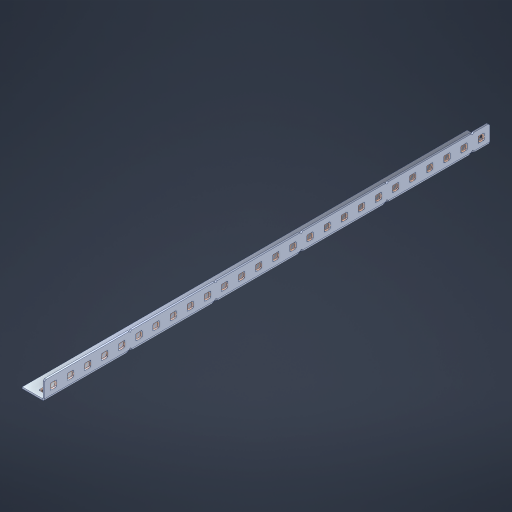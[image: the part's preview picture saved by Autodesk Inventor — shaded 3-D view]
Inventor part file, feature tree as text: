
AUTODESK INVENTOR PART (.ipt)
format: ipt  version: 2023 (Build 270158000, 158)  size: 876,544 bytes
history: native  units: in
note: dims shown in document units (in); Inventor stores cm internally (conversion verified against a paired STEP export)
features: other x57, extrude x51, sheet_metal_op x10, sketch x8, mirror x1, pattern_linear x1, chamfer x1
ambient origin geometry x8: Origin, YZ Plane, XZ Plane, XY Plane, X Axis, Y Axis, Z Axis, Center Point
bodies: Solid1 (feature_tree), Body (feature_tree)
feature tree (129):
  other  "Flange Pattern Plane"
  sheet_metal_op  "Flange Pattern"
  sheet_metal_op  "Body Pattern"
  other  "Arc Length"
  mirror  "Notch Mirror"
  pattern_linear  "Notch Pattern"  Spacing1=0.1875in  [1 undecoded]
  chamfer  "End Chamfer"
  extrude  "Half Cut"  Depth=0.0469in
  sketch  "Sketch1"  dims[d0=2.5in]
  other  "Plate1"
  sketch  "Sketch2"  dims[d1=13.0in]
  other  "Plate2"
  sheet_metal_op  "Bend1"
  sheet_metal_op  "Corner1"
  sketch  "Sketch3"  dims[d2=0.0469in]
  other  "Flange Pattern Sketch"
  sketch  "Sketch7"  dims[d3=0.0469in]
  other  "Srf1"
  other  "Srf2"
  sketch  "Sketch8"  dims[d4=0.0234in]
  sketch  "Sketch9"  dims[d5=0.0938in]
  other  "Srf91"
  sheet_metal_op  "Body Pattern Sketch"
  other  "Srf92"
  sketch  "Sketch13"  dims[d6=0.0469in]
  sketch  "Sketch14"  dims[d7=0.5in d8=90.0deg d9=0.0312in d10=0.1875in d11=0.0469in d12=0.0469in d16=0.182in d17=0.02in d18=0.0469in d19=0.0in d20=0.25in d21=0.25in d46=0.172in d47=1.0in d48=0.0in d49=0.182in d50=0.02in d51=0.25in d52=0.25in d53=0.0469in d54=0.0in d55=0.172in d56=1.0in d57=0.0in d60=10.2362in d62=0.5in d63=0.3937in d65=0.5in d85=0.1227in d86=0.1659in d88=0.04in d89=0.0469in d90=0.0in d91=0.04in d92=0.0491in d95=2.5in d96=0.04in d97=0.25in d98=45.0deg d101=0.0in d102=2.497in d131=0.5in d132=10.2362in d134=0.5in d139=0.5in]
  other  "Srf856"
  other  "Srf1310"
  other  "Srf1311"
  other  "Srf1312"
  other  "Srf1376"
  other  "Srf1377"
  other  "Srf1728"
  other  "Srf1755"
  other  "Srf1878"
  other  "Srf1879"
  other  "Srf1880"
  other  "Srf1881"
  other  "Srf1882"
  other  "Srf1883"
  other  "Srf1884"
  other  "Srf1885"
  other  "Srf1886"
  other  "Srf1887"
  other  "Srf1888"
  other  "Srf1889"
  other  "Srf1890"
  other  "Srf1891"
  other  "Srf1892"
  other  "Srf1893"
  other  "Srf1894"
  other  "Srf1895"
  other  "Srf1896"
  other  "Srf1897"
  other  "Srf1942"
  other  "Srf1943"
  other  "Srf1944"
  other  "Srf1945"
  other  "Srf1946"
  other  "Srf1947"
  other  "Srf1948"
  other  "Srf1949"
  other  "Srf1950"
  other  "Srf1951"
  other  "Srf1952"
  other  "Srf1953"
  other  "Srf1954"
  other  "Srf1955"
  other  "Srf1956"
  other  "Srf1957"
  other  "Srf1958"
  other  "Srf1959"
  other  "Srf1960"
  other  "Srf1961"
  sheet_metal_op  "Flange Stamp"
  sheet_metal_op  "Flange Circle"
  sheet_metal_op  "Body Stamp"
  sheet_metal_op  "Body Circle"
  sheet_metal_op  "Notch"
  extrude  "ExtrusionSrf2"  Depth=0.0469in
  extrude  "ExtrusionSrf92"  Depth=0.5in
  extrude  "ExtrusionSrf856"  Depth=0.02in
  extrude  "ExtrusionSrf1310"  Depth=0.0469in
  extrude  "ExtrusionSrf1311"  TaperAngle=0.0deg  [1 undecoded]
  extrude  "ExtrusionSrf1312"  Depth=0.5in
  extrude  "ExtrusionSrf1376"  Depth=0.5in
  extrude  "ExtrusionSrf1377"  Depth=0.5in
  extrude  "ExtrusionSrf1728"  Depth=0.5in TaperAngle=0.0deg
  extrude  "ExtrusionSrf1755"  Depth=0.5in
  extrude  "ExtrusionSrf1878"  Depth=0.02in
  extrude  "ExtrusionSrf1879"  Depth=0.5in
  extrude  "ExtrusionSrf1880"  Depth=0.5in
  extrude  "ExtrusionSrf1881"  Depth=0.0469in
  extrude  "ExtrusionSrf1882"  TaperAngle=0.0deg  [1 undecoded]
  extrude  "ExtrusionSrf1883"  Depth=0.5in
  extrude  "ExtrusionSrf1884"  Depth=0.5in TaperAngle=0.0deg
  extrude  "ExtrusionSrf1885"  Depth=0.5in
  extrude  "ExtrusionSrf1886"  Depth=0.5in
  extrude  "ExtrusionSrf1887"  Depth=0.5in
  extrude  "ExtrusionSrf1888"  Depth=0.5in
  extrude  "ExtrusionSrf1889"  Depth=0.5in
  extrude  "ExtrusionSrf1890"  Depth=0.0469in
  extrude  "ExtrusionSrf1891"  TaperAngle=0.0deg  [1 undecoded]
  extrude  "ExtrusionSrf1892"  Depth=0.5in
  extrude  "ExtrusionSrf1893"  Depth=0.5in
  extrude  "ExtrusionSrf1894"  Depth=0.5in
  extrude  "ExtrusionSrf1895"  Depth=0.5in TaperAngle=45.0deg
  extrude  "ExtrusionSrf1896"  TaperAngle=0.0deg  [1 undecoded]
  extrude  "ExtrusionSrf1897"  Depth=0.5in
  extrude  "ExtrusionSrf1942"  Depth=0.5in
  extrude  "ExtrusionSrf1943"  Depth=0.5in
  extrude  "ExtrusionSrf1944"  Depth=0.5in
  extrude  "ExtrusionSrf1945"  Depth=0.5in
  extrude  "ExtrusionSrf1946"  [1 undecoded]
  extrude  "ExtrusionSrf1947"  [1 undecoded]
  extrude  "ExtrusionSrf1948"  [1 undecoded]
  extrude  "ExtrusionSrf1949"  [1 undecoded]
  extrude  "ExtrusionSrf1950"  [1 undecoded]
  extrude  "ExtrusionSrf1951"  [1 undecoded]
  extrude  "ExtrusionSrf1952"  [1 undecoded]
  extrude  "ExtrusionSrf1953"  [1 undecoded]
  extrude  "ExtrusionSrf1954"  [1 undecoded]
  extrude  "ExtrusionSrf1955"  [1 undecoded]
  extrude  "ExtrusionSrf1956"  [1 undecoded]
  extrude  "ExtrusionSrf1957"  [1 undecoded]
  extrude  "ExtrusionSrf1958"  [1 undecoded]
  extrude  "ExtrusionSrf1959"  [1 undecoded]
  extrude  "ExtrusionSrf1960"  [1 undecoded]
  extrude  "ExtrusionSrf1961"  [1 undecoded]
note: 21 required parameter values undecoded (feature->parameter linkage not recoverable at this tier; creation-order binding heuristic only, values carry confidence <= 0.55)
